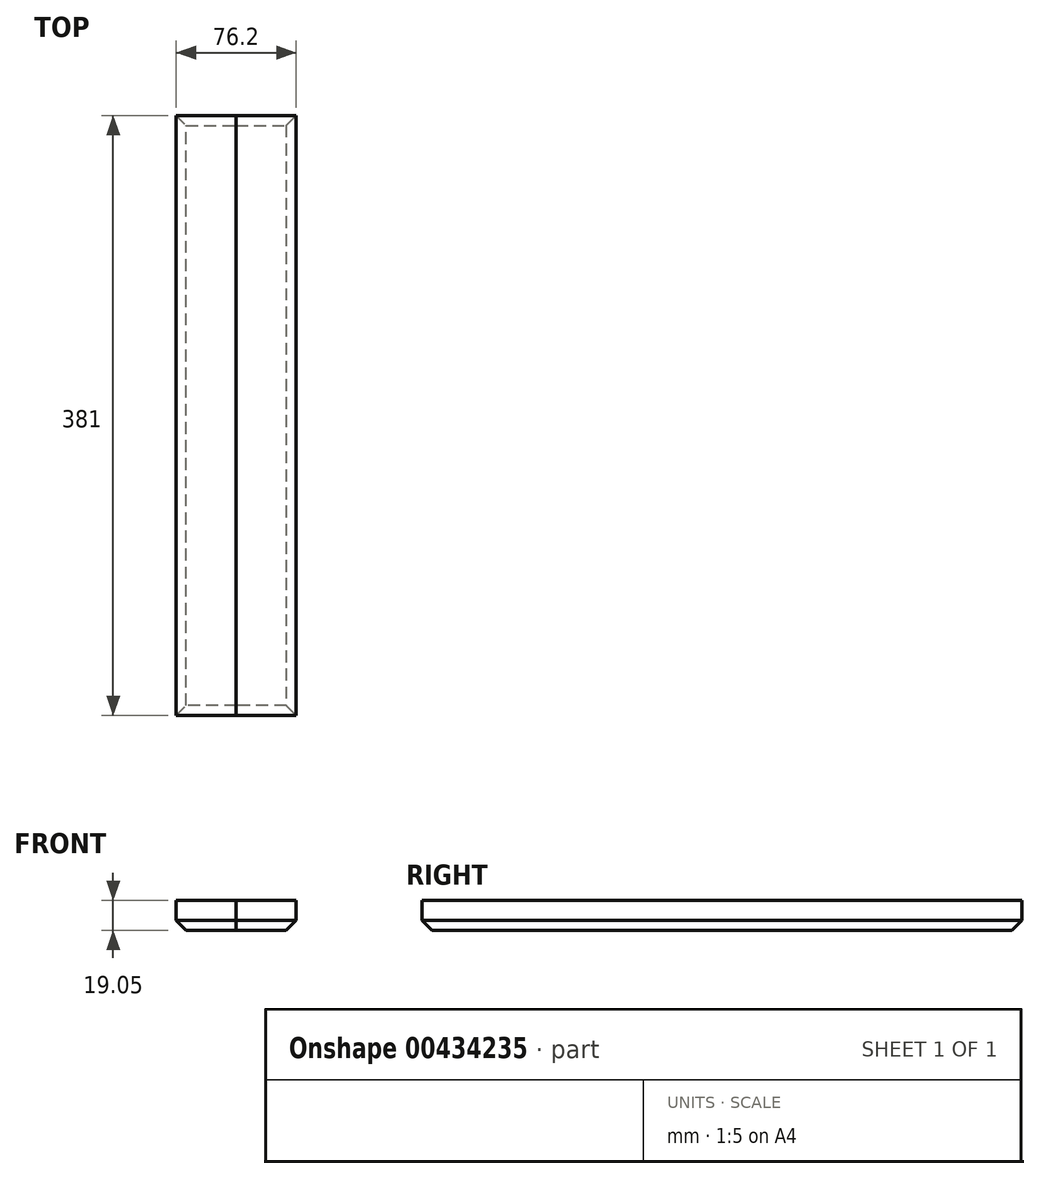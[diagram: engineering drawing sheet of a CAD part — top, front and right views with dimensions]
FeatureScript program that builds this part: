
annotation { "Feature Type Name" : "Feature", "Feature Type Description" : "" }
export const myFeature = defineFeature(function(context is Context, id is Id, definition is map)
    precondition{}
    {
        {
            var Q0;
            Q0=qCreatedBy(makeId("Front.planeOp"),FACE);
            var sketch = newSketch(context, id + "F0", { "sketchPlane" : qUnion([Q0])});
            skLineSegment(sketch, "E0.bottom", {"start": v(0, 0) * mm, "end": v(38.1, 0) * mm});
            skLineSegment(sketch, "E0.top", {"start": v(0, 19.05) * mm, "end": v(38.1, 19.05) * mm});
            skLineSegment(sketch, "E0.left", {"start": v(0, 0) * mm, "end": v(0, 19.05) * mm});
            skLineSegment(sketch, "E0.right", {"start": v(38.1, 0) * mm, "end": v(38.1, 19.05) * mm});
            skSolve(sketch);
        }
        {
            var Q0;
            Q0 = qSketchRegion(id + "F0", true);
            extrude(context, id + "F1", {"entities" : qUnion([Q0]), "depth" : 381 * mm});
        }
        {
            var Q0;
            Q0=makeQuery(id+"F1.opExtrude","SWEPT_FACE",FACE,{"disambiguationData":[OSD([sQuery(id+"F0.wireOp",EDGE,"E0.top")])]});
            var sketch = newSketch(context, id + "F2", { "sketchPlane" : qUnion([Q0])});
            skLineSegment(sketch, "E1.bottom", {"start": v(38.1, 0) * mm, "end": v(76.2, 0) * mm});
            skLineSegment(sketch, "E1.top", {"start": v(38.1, -381) * mm, "end": v(76.2, -381) * mm});
            skLineSegment(sketch, "E1.left", {"start": v(38.1, 0) * mm, "end": v(38.1, -381) * mm});
            skLineSegment(sketch, "E1.right", {"start": v(76.2, 0) * mm, "end": v(76.2, -381) * mm});
            skSolve(sketch);
        }
        {
            var Q0;
            Q0 = qSketchRegion(id + "F2", true);
            extrude(context, id + "F3", {"entities" : qUnion([Q0]), "depth" : -19.05 * mm});
        }
        {
            var Q0;
            Q0=makeQuery(id+"F1.opExtrude","SWEPT_EDGE",EDGE,{"disambiguationData":[OSD([sQuery(id+"F0.wireOp",EDGE,"E0.bottom"),sQuery(id+"F0.wireOp",EDGE,"E0.left")])]});
            var Q1;
            Q1=makeQuery(id+"F3.opExtrude","CAP_EDGE",EDGE,{"disambiguationData":[OSD([sQuery(id+"F2.wireOp",EDGE,"E1.right")])],"isStart":false});
            var Q2;
            Q2=makeQuery(id+"F3.opExtrude","CAP_EDGE",EDGE,{"disambiguationData":[OSD([sQuery(id+"F2.wireOp",EDGE,"E1.top")])],"isStart":false});
            var Q3;
            Q3=makeQuery(id+"F1.opExtrude","CAP_EDGE",EDGE,{"disambiguationData":[OSD([sQuery(id+"F0.wireOp",EDGE,"E0.bottom")])],"isStart":false});
            var Q4;
            Q4=makeQuery(id+"F3.opExtrude","CAP_EDGE",EDGE,{"disambiguationData":[OSD([sQuery(id+"F2.wireOp",EDGE,"E1.bottom")])],"isStart":false});
            var Q5;
            Q5=makeQuery(id+"F1.opExtrude","CAP_EDGE",EDGE,{"disambiguationData":[OSD([sQuery(id+"F0.wireOp",EDGE,"E0.bottom")])],"isStart":true});
            chamfer(context, id + "F4", {"entities" : qUnion([Q0, Q1, Q2, Q3, Q4, Q5]), "width" : 6.35 * mm, "tangentPropagation" : true});
        }
    });
